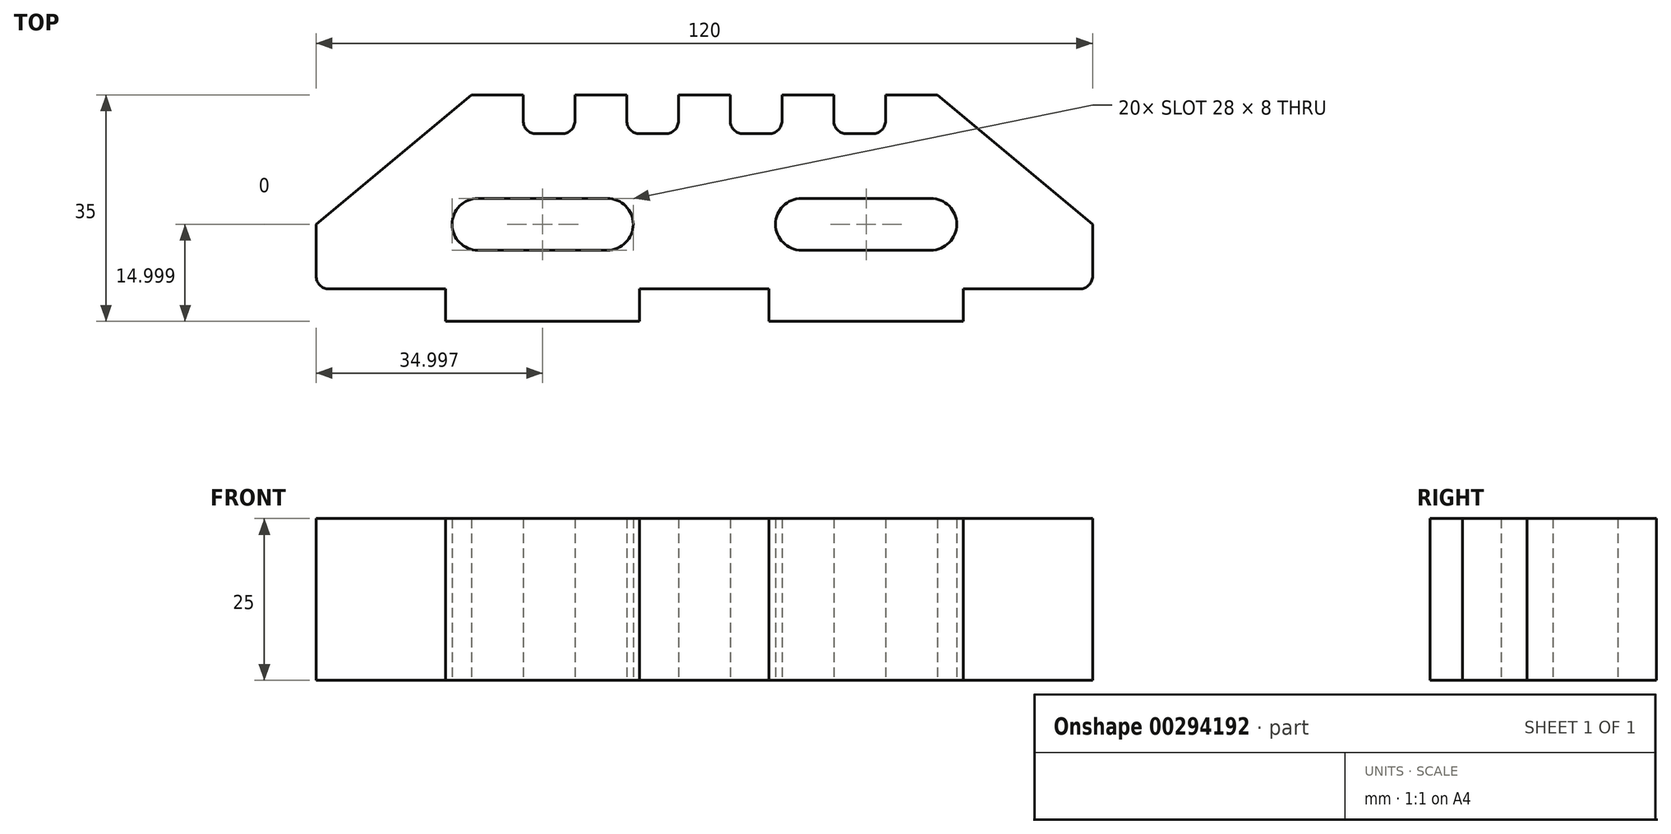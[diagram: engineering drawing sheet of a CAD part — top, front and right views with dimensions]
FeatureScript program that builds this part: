
annotation { "Feature Type Name" : "Feature", "Feature Type Description" : "" }
export const myFeature = defineFeature(function(context is Context, id is Id, definition is map)
    precondition{}
    {
        {
            var Q0;
            Q0=qCreatedBy(makeId("Top.planeOp"),FACE);
            var sketch = newSketch(context, id + "F0", { "sketchPlane" : qUnion([Q0])});
            skLineSegment(sketch, "E0", {"start": v(-67.01, -18.01) * mm, "end": v(-49.01, -18.01) * mm});
            skLineSegment(sketch, "E1", {"start": v(-49.01, -18.01) * mm, "end": v(-49.01, -23.01) * mm});
            skLineSegment(sketch, "E2", {"start": v(-49.01, -23.01) * mm, "end": v(-19.01, -23.01) * mm});
            skLineSegment(sketch, "E3", {"start": v(-19.01, -23.01) * mm, "end": v(-19.01, -18.01) * mm});
            skLineSegment(sketch, "E4", {"start": v(-19.01, -18.01) * mm, "end": v(0.99, -18.01) * mm});
            skLineSegment(sketch, "E5", {"start": v(0.99, -18.01) * mm, "end": v(0.99, -23.01) * mm});
            skLineSegment(sketch, "E6", {"start": v(0.99, -23.01) * mm, "end": v(30.99, -23.01) * mm});
            skLineSegment(sketch, "E7", {"start": v(30.99, -23.01) * mm, "end": v(30.99, -18.01) * mm});
            skLineSegment(sketch, "E8", {"start": v(30.99, -18.01) * mm, "end": v(48.99, -18.01) * mm});
            skLineSegment(sketch, "E9", {"start": v(-69.01, -16.01) * mm, "end": v(-69.01, -8.01) * mm});
            skLineSegment(sketch, "E10", {"start": v(50.99, -16.01) * mm, "end": v(50.99, -8.01) * mm});
            skLineSegment(sketch, "E11", {"start": v(-69.01, -8.01) * mm, "end": v(-45.01, 11.99) * mm});
            skLineSegment(sketch, "E12", {"start": v(-45.01, 11.99) * mm, "end": v(-37.01, 11.99) * mm});
            skLineSegment(sketch, "E13", {"start": v(-37.01, 11.99) * mm, "end": v(-37.01, 7.99) * mm});
            skLineSegment(sketch, "E14", {"start": v(-35.01, 5.99) * mm, "end": v(-31.01, 5.99) * mm});
            skLineSegment(sketch, "E15", {"start": v(-29.01, 7.99) * mm, "end": v(-29.01, 11.99) * mm});
            skLineSegment(sketch, "E16", {"start": v(-29.01, 11.99) * mm, "end": v(-21.01, 11.99) * mm});
            skLineSegment(sketch, "E17", {"start": v(-21.01, 11.99) * mm, "end": v(-21.01, 7.99) * mm});
            skLineSegment(sketch, "E18", {"start": v(-19.01, 5.99) * mm, "end": v(-15.01, 5.99) * mm});
            skLineSegment(sketch, "E19", {"start": v(-13.01, 7.99) * mm, "end": v(-13.01, 11.99) * mm});
            skLineSegment(sketch, "E20", {"start": v(-13.01, 11.99) * mm, "end": v(-5.01, 11.99) * mm});
            skLineSegment(sketch, "E21", {"start": v(-5.01, 11.99) * mm, "end": v(-5.01, 7.99) * mm});
            skLineSegment(sketch, "E22", {"start": v(-3.01, 5.99) * mm, "end": v(0.99, 5.99) * mm});
            skLineSegment(sketch, "E23", {"start": v(2.99, 7.99) * mm, "end": v(2.99, 11.99) * mm});
            skLineSegment(sketch, "E24", {"start": v(2.99, 11.99) * mm, "end": v(10.99, 11.99) * mm});
            skLineSegment(sketch, "E25", {"start": v(10.99, 11.99) * mm, "end": v(10.99, 7.99) * mm});
            skLineSegment(sketch, "E26", {"start": v(12.99, 5.99) * mm, "end": v(16.99, 5.99) * mm});
            skLineSegment(sketch, "E27", {"start": v(18.99, 7.99) * mm, "end": v(18.99, 11.99) * mm});
            skLineSegment(sketch, "E28", {"start": v(18.99, 11.99) * mm, "end": v(26.99, 11.99) * mm});
            skLineSegment(sketch, "E29", {"start": v(26.99, 11.99) * mm, "end": v(50.99, -8.01) * mm});
            skPoint(sketch, "E30.visualSharp", {"position": v(-37.01, 5.99) * mm});
            skArc(sketch, "E30.filletArc", {"start": v(-37.01, 7.99) * mm, "mid": v(-36.43, 6.58) * mm, "end": v(-35.01, 5.99) * mm});
            skPoint(sketch, "E31.visualSharp", {"position": v(-29.01, 5.99) * mm});
            skArc(sketch, "E31.filletArc", {"start": v(-31.01, 5.99) * mm, "mid": v(-29.6, 6.58) * mm, "end": v(-29.01, 7.99) * mm});
            skPoint(sketch, "E32.visualSharp", {"position": v(-21.01, 5.99) * mm});
            skArc(sketch, "E32.filletArc", {"start": v(-21.01, 7.99) * mm, "mid": v(-20.43, 6.58) * mm, "end": v(-19.01, 5.99) * mm});
            skPoint(sketch, "E33.visualSharp", {"position": v(-13.01, 5.99) * mm});
            skArc(sketch, "E33.filletArc", {"start": v(-15.01, 5.99) * mm, "mid": v(-13.6, 6.58) * mm, "end": v(-13.01, 7.99) * mm});
            skPoint(sketch, "E34.visualSharp", {"position": v(-5.01, 5.99) * mm});
            skArc(sketch, "E34.filletArc", {"start": v(-5.01, 7.99) * mm, "mid": v(-4.43, 6.58) * mm, "end": v(-3.01, 5.99) * mm});
            skPoint(sketch, "E35.visualSharp", {"position": v(2.99, 5.99) * mm});
            skArc(sketch, "E35.filletArc", {"start": v(0.99, 5.99) * mm, "mid": v(2.4, 6.58) * mm, "end": v(2.99, 7.99) * mm});
            skPoint(sketch, "E36.visualSharp", {"position": v(10.99, 5.99) * mm});
            skArc(sketch, "E36.filletArc", {"start": v(10.99, 7.99) * mm, "mid": v(11.57, 6.58) * mm, "end": v(12.99, 5.99) * mm});
            skPoint(sketch, "E37.visualSharp", {"position": v(18.99, 5.99) * mm});
            skArc(sketch, "E37.filletArc", {"start": v(16.99, 5.99) * mm, "mid": v(18.4, 6.58) * mm, "end": v(18.99, 7.99) * mm});
            skLineSegment(sketch, "E38", {"start": v(-9.01, 23.84) * mm, "end": v(-9.01, 11.99) * mm});
            skLineSegment(sketch, "E39", {"start": v(1.99, -8.01) * mm, "end": v(1.99, -7.36) * mm});
            skLineSegment(sketch, "E40", {"start": v(1.99, -8.01) * mm, "end": v(1.99, -8.01) * mm});
            skLineSegment(sketch, "E41", {"start": v(5.99, -4.01) * mm, "end": v(25.99, -4.01) * mm});
            skLineSegment(sketch, "E42", {"start": v(5.99, -12.01) * mm, "end": v(25.99, -12.01) * mm});
            skLineSegment(sketch, "E43", {"start": v(29.99, -8.01) * mm, "end": v(29.99, -8.01) * mm});
            skPoint(sketch, "E44.visualSharp", {"position": v(1.99, -4.01) * mm});
            skArc(sketch, "E44.filletArc", {"start": v(5.99, -4.01) * mm, "mid": v(3.16, -5.18) * mm, "end": v(1.99, -8.01) * mm});
            skPoint(sketch, "E45.visualSharp", {"position": v(1.99, -12.01) * mm});
            skArc(sketch, "E45.filletArc", {"start": v(1.99, -8.01) * mm, "mid": v(3.16, -10.84) * mm, "end": v(5.99, -12.01) * mm});
            skPoint(sketch, "E46.end.orphan", {"position": v(1.99, -7.36) * mm});
            skPoint(sketch, "E47.visualSharp", {"position": v(29.99, -4.01) * mm});
            skArc(sketch, "E47.filletArc", {"start": v(29.99, -8.01) * mm, "mid": v(28.81, -5.18) * mm, "end": v(25.99, -4.01) * mm});
            skPoint(sketch, "E48.visualSharp", {"position": v(29.99, -12.01) * mm});
            skArc(sketch, "E48.filletArc", {"start": v(25.99, -12.01) * mm, "mid": v(28.81, -10.84) * mm, "end": v(29.99, -8.01) * mm});
            skLineSegment(sketch, "E49", {"start": v(-20.01, -8.01) * mm, "end": v(-20.01, -8.01) * mm});
            skLineSegment(sketch, "E50", {"start": v(-24.01, -4.01) * mm, "end": v(-44.01, -4.01) * mm});
            skLineSegment(sketch, "E51", {"start": v(-24.01, -12.01) * mm, "end": v(-44.01, -12.01) * mm});
            skLineSegment(sketch, "E52", {"start": v(-48.01, -8.01) * mm, "end": v(-48.01, -8.01) * mm});
            skPoint(sketch, "E53.visualSharp", {"position": v(-20.01, -4.01) * mm});
            skArc(sketch, "E53.filletArc", {"start": v(-20.01, -8.01) * mm, "mid": v(-21.19, -5.18) * mm, "end": v(-24.01, -4.01) * mm});
            skPoint(sketch, "E54.visualSharp", {"position": v(-20.01, -12.01) * mm});
            skArc(sketch, "E54.filletArc", {"start": v(-24.01, -12.01) * mm, "mid": v(-21.19, -10.84) * mm, "end": v(-20.01, -8.01) * mm});
            skPoint(sketch, "E55.visualSharp", {"position": v(-48.01, -12.01) * mm});
            skArc(sketch, "E55.filletArc", {"start": v(-48.01, -8.01) * mm, "mid": v(-46.84, -10.84) * mm, "end": v(-44.01, -12.01) * mm});
            skPoint(sketch, "E56.visualSharp", {"position": v(-48.01, -4.01) * mm});
            skArc(sketch, "E56.filletArc", {"start": v(-44.01, -4.01) * mm, "mid": v(-46.84, -5.18) * mm, "end": v(-48.01, -8.01) * mm});
            skPoint(sketch, "E57.end.orphan", {"position": v(-20.01, -8.16) * mm});
            skPoint(sketch, "E58.orphan", {"position": v(-9.01, -18.01) * mm});
            skPoint(sketch, "E59.visualSharp", {"position": v(-69.01, -18.01) * mm});
            skArc(sketch, "E59.filletArc", {"start": v(-69.01, -16.01) * mm, "mid": v(-68.43, -17.42) * mm, "end": v(-67.01, -18.01) * mm});
            skPoint(sketch, "E60.visualSharp", {"position": v(50.99, -18.01) * mm});
            skArc(sketch, "E60.filletArc", {"start": v(48.99, -18.01) * mm, "mid": v(50.4, -17.42) * mm, "end": v(50.99, -16.01) * mm});
            skSolve(sketch);
        }
        {
            var Q0;
            Q0 = qSketchRegion(id + "F0", true);
            extrude(context, id + "F1", {"entities" : qUnion([Q0]), "depth" : 25 * mm});
        }
    });
